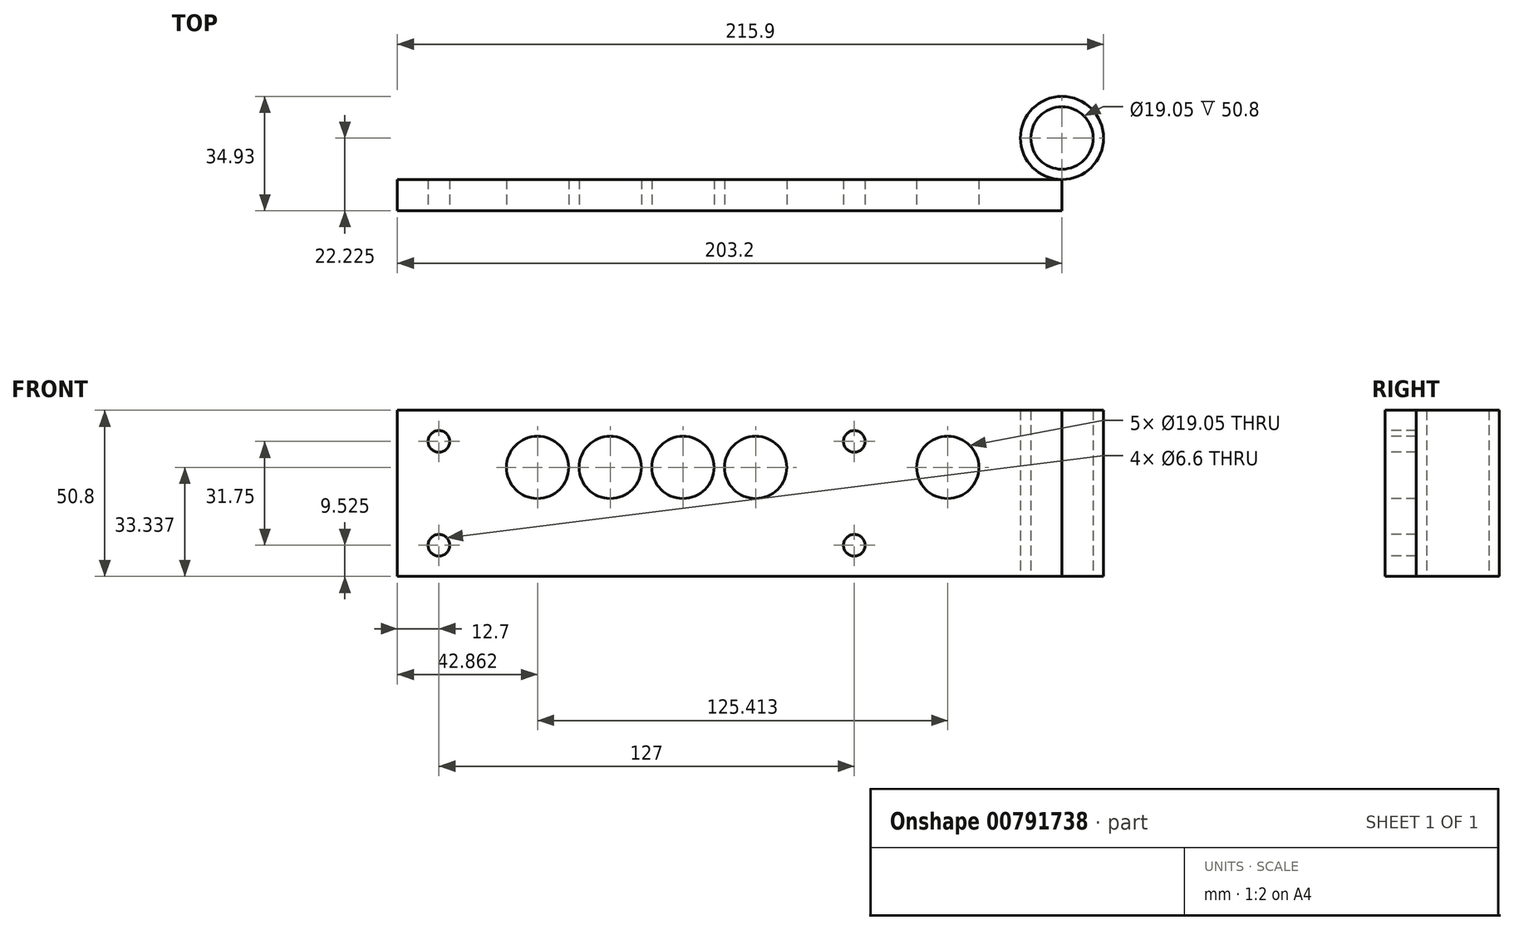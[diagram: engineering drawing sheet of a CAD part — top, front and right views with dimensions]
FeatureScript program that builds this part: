
annotation { "Feature Type Name" : "Feature", "Feature Type Description" : "" }
export const myFeature = defineFeature(function(context is Context, id is Id, definition is map)
    precondition{}
    {
        {
            var Q0;
            Q0=qCreatedBy(makeId("Front.planeOp"),FACE);
            var sketch = newSketch(context, id + "F0", { "sketchPlane" : qUnion([Q0])});
            skLineSegment(sketch, "E0.bottom", {"start": v(0, 0) * mm, "end": v(203.2, 0) * mm});
            skLineSegment(sketch, "E0.top", {"start": v(0, 50.8) * mm, "end": v(203.2, 50.8) * mm});
            skLineSegment(sketch, "E0.left", {"start": v(0, 0) * mm, "end": v(0, 50.8) * mm});
            skLineSegment(sketch, "E0.right", {"start": v(203.2, 0) * mm, "end": v(203.2, 50.8) * mm});
            skCircle(sketch, "E1", {"center": v(12.7, 9.53) * mm, "radius": 3.3 * mm});
            skCircle(sketch, "E2.0.1.0", {"center": v(12.7, 41.27) * mm, "radius": 3.3 * mm});
            skCircle(sketch, "E2.1.0.0", {"center": v(139.7, 9.53) * mm, "radius": 3.3 * mm});
            skCircle(sketch, "E2.1.1.0", {"center": v(139.7, 41.27) * mm, "radius": 3.3 * mm});
            skLineSegment(sketch, "E2.direction1", {"start": v(12.7, 9.53) * mm, "end": v(139.7, 9.53) * mm, "construction": true});
            skLineSegment(sketch, "E2.direction2", {"start": v(12.7, 9.52) * mm, "end": v(12.7, 41.27) * mm, "construction": true});
            skCircle(sketch, "E3", {"center": v(42.86, 33.34) * mm, "radius": 9.53 * mm});
            skCircle(sketch, "E4.1.0.0", {"center": v(65.09, 33.34) * mm, "radius": 9.53 * mm});
            skCircle(sketch, "E4.2.0.0", {"center": v(87.31, 33.34) * mm, "radius": 9.53 * mm});
            skCircle(sketch, "E4.3.0.0", {"center": v(109.54, 33.34) * mm, "radius": 9.53 * mm});
            skLineSegment(sketch, "E4.direction1", {"start": v(42.86, 33.34) * mm, "end": v(65.09, 33.34) * mm, "construction": true});
            skCircle(sketch, "E5", {"center": v(168.28, 33.34) * mm, "radius": 9.53 * mm});
            skSolve(sketch);
        }
        {
            var Q0;
            Q0=qSketchRegion(id+"F0",true);
            extrude(context, id + "F1", {"entities" : qUnion([Q0]), "oppositeDirection" : true, "depth" : 9.52 * mm, "offsetDistance" : 25.4 * mm});
        }
        {
            var Q0;
            Q0=qCreatedBy(makeId("Top.planeOp"),FACE);
            var sketch = newSketch(context, id + "F2", { "sketchPlane" : qUnion([Q0])});
            skCircle(sketch, "E6", {"center": v(203.2, 22.23) * mm, "radius": 12.7 * mm});
            skCircle(sketch, "E7", {"center": v(203.2, 22.23) * mm, "radius": 9.53 * mm});
            skSolve(sketch);
        }
        {
            var Q0;
            Q0=qSketchRegion(id+"F2",true);
            extrude(context, id + "F3", {"entities" : qUnion([Q0]), "depth" : 50.8 * mm, "offsetDistance" : 25.4 * mm});
        }
    });
